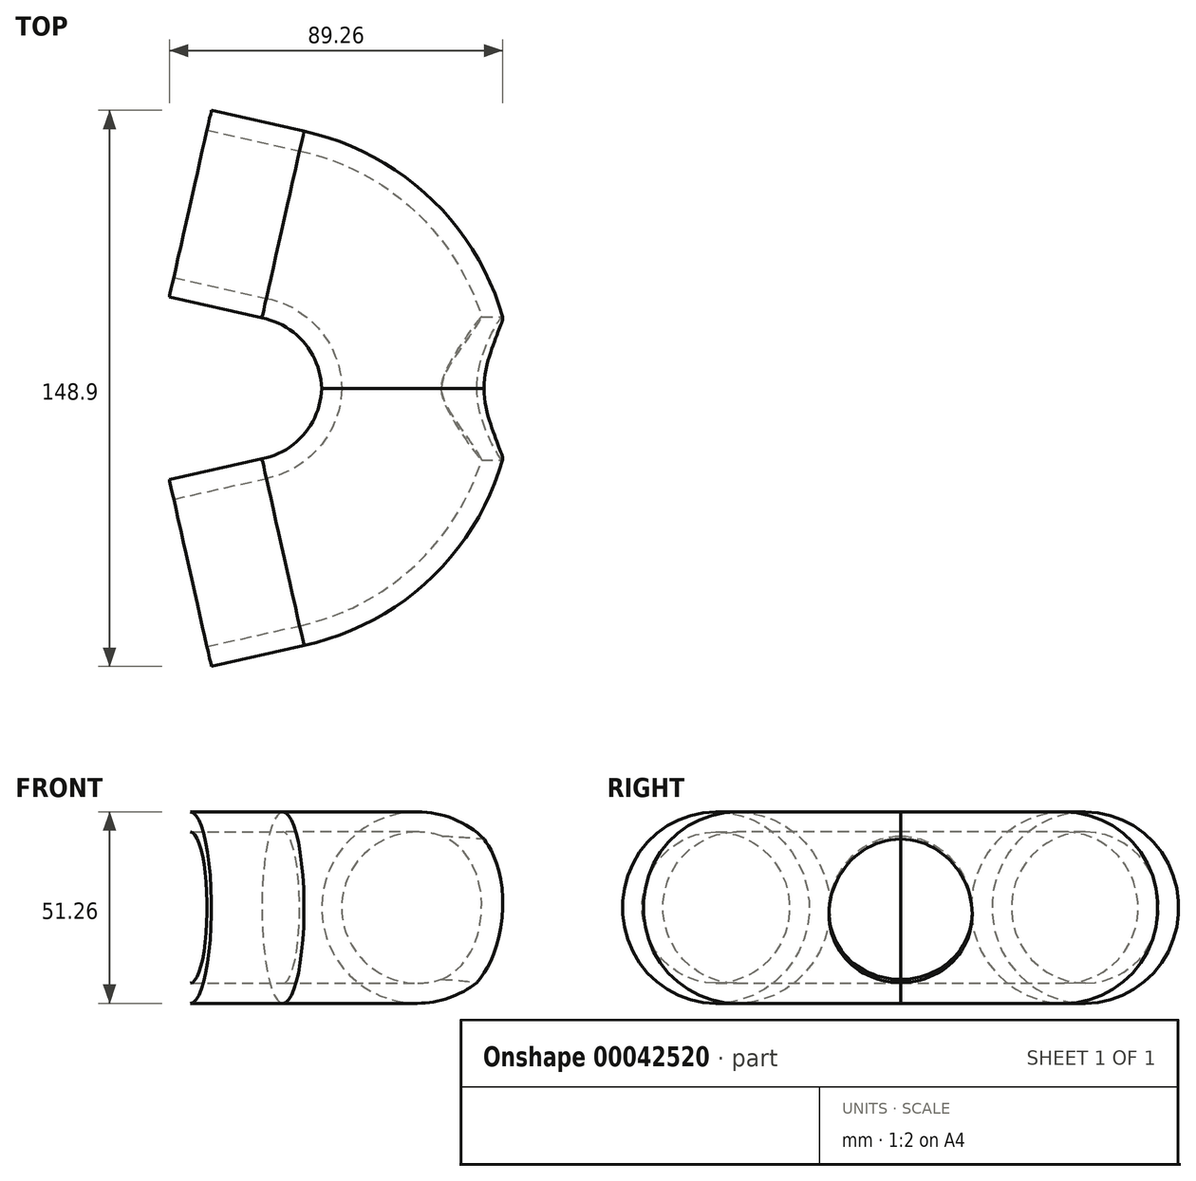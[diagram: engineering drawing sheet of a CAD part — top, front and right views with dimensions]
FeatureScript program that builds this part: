
annotation { "Feature Type Name" : "Feature", "Feature Type Description" : "" }
export const myFeature = defineFeature(function(context is Context, id is Id, definition is map)
    precondition{}
    {
        {
            var Q0;
            Q0=qCreatedBy(makeId("Front.planeOp"),FACE);
            var sketch = newSketch(context, id + "F0", { "sketchPlane" : qUnion([Q0])});
            skCircle(sketch, "E0", {"center": v(0, 0) * mm, "radius": 25.63 * mm});
            skCircle(sketch, "E1", {"center": v(0, 0) * mm, "radius": 20.24 * mm});
            skSolve(sketch);
        }
        {
            var Q0;
            Q0=qCreatedBy(makeId("Top.planeOp"),FACE);
            var sketch = newSketch(context, id + "F1", { "sketchPlane" : qUnion([Q0])});
            skArc(sketch, "E2", {"start": v(-35.98, -43.86) * mm, "mid": v(-10.3, -28.24) * mm, "end": v(0, 0) * mm});
            skSolve(sketch);
        }
        {
            var Q0;
            Q0=makeQuery(id+"F0.imprint","IMPRINT",FACE,{"disambiguationData":[TD([[makeQuery(id+"F0.imprint","IMPRINT",EDGE,{"derivedFrom":sQuery(id+"F0.wireOp",EDGE,"E0")}),1.0]])]});
            var Q1;
            Q1=sQuery(id+"F1.wireOp",EDGE,"E2");
            sweep(context, id + "F2", {"profiles" : qUnion([Q0]), "path" : qUnion([Q1])});
        }
        {
            var Q0;
            Q0=makeQuery(id+"F2.opSweep","CAP_FACE",FACE,{"disambiguationData":[OSD([sQuery(id+"F0.wireOp",EDGE,"E0"),sQuery(id+"F0.wireOp",EDGE,"E1"),sQuery(id+"F1.wireOp",VERTEX,"E2.start")])],"isStart":false});
            extrude(context, id + "F3", {"entities" : qUnion([Q0]), "operationType" : NewBodyOperationType.ADD, "depth" : 25.4 * mm});
        }
        {
            var Q0;
            Q0=makeQuery(id+"F2.opSweep","SWEPT_BODY",BODY,{"disambiguationData":[OSD([sQuery(id+"F0.wireOp",EDGE,"E0"),sQuery(id+"F0.wireOp",EDGE,"E1"),sQuery(id+"F1.wireOp",EDGE,"E2")])]});
            var Q1;
            Q1=qCreatedBy(makeId("Front.planeOp"),FACE);
            mirror(context, id + "F4", {"operationType" : NewBodyOperationType.ADD, "entities" : qUnion([Q0]), "mirrorPlane" : qUnion([Q1])});
        }
        {
            var Q0;
            Q0=qCreatedBy(makeId("Right.planeOp"),FACE);
            var sketch = newSketch(context, id + "F5", { "sketchPlane" : qUnion([Q0])});
            skCircle(sketch, "E3", {"center": v(0, 0) * mm, "radius": 19.18 * mm});
            skSolve(sketch);
        }
        {
            var Q0;
            Q0=qCreatedBy(makeId("Front.planeOp"),FACE);
            var sketch = newSketch(context, id + "F6", { "sketchPlane" : qUnion([Q0])});
            skArc(sketch, "E4", {"start": v(65.49, -19) * mm, "mid": v(34.21, -4.43) * mm, "end": v(0, 0) * mm});
            skSolve(sketch);
        }
        {
            var Q0;
            Q0 = qSketchRegion(id + "F5", true);
            var Q1;
            Q1 = qConstructionFilter(qBodyType(qCreatedBy(id + "F6" ,EDGE), BodyType.WIRE), ConstructionObject.NO);
            sweep(context, id + "F7", {"operationType" : NewBodyOperationType.REMOVE, "profiles" : qUnion([Q0]), "path" : qUnion([Q1])});
        }
    });
